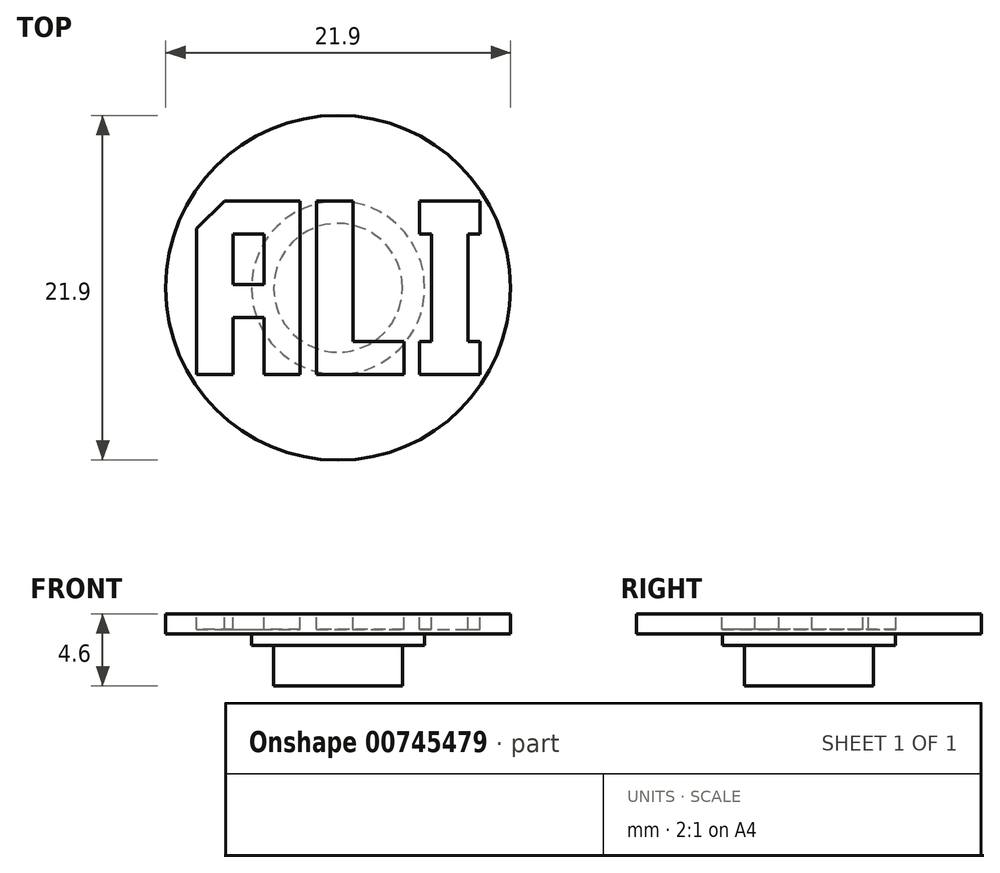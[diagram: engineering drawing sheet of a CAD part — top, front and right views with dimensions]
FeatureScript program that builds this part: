
annotation { "Feature Type Name" : "Feature", "Feature Type Description" : "" }
export const myFeature = defineFeature(function(context is Context, id is Id, definition is map)
    precondition{}
    {
        {
            var Q0;
            Q0=qCreatedBy(makeId("Top.planeOp"),FACE);
            var sketch = newSketch(context, id + "F0", { "sketchPlane" : qUnion([Q0])});
            skCircle(sketch, "E0", {"center": v(0, 0) * mm, "radius": 4.1 * mm});
            skSolve(sketch);
        }
        {
            var Q0;
            Q0 = qSketchRegion(id + "F0", true);
            extrude(context, id + "F1", {"entities" : qUnion([Q0]), "depth" : 2.6 * mm, "offsetDistance" : 25.4 * mm});
        }
        {
            var Q0;
            Q0=makeQuery(id+"F1.opExtrude","CAP_FACE",FACE,{"disambiguationData":[OSD([sQuery(id+"F0.wireOp",EDGE,"E0")])],"isStart":false});
            var sketch = newSketch(context, id + "F2", { "sketchPlane" : qUnion([Q0])});
            skCircle(sketch, "E1", {"center": v(0, 0) * mm, "radius": 5.5 * mm});
            skSolve(sketch);
        }
        {
            var Q0;
            Q0 = qSketchRegion(id + "F2", true);
            extrude(context, id + "F3", {"entities" : qUnion([Q0]), "operationType" : NewBodyOperationType.ADD, "depth" : 0.7 * mm, "offsetDistance" : 25.4 * mm});
        }
        {
            var Q0;
            Q0=makeQuery(id+"F3.opExtrude","CAP_FACE",FACE,{"disambiguationData":[OSD([sQuery(id+"F2.wireOp",EDGE,"E1")])],"isStart":false});
            var sketch = newSketch(context, id + "F4", { "sketchPlane" : qUnion([Q0])});
            skCircle(sketch, "E2", {"center": v(0, 0) * mm, "radius": 10.95 * mm});
            skSolve(sketch);
        }
        {
            var Q0;
            Q0 = qSketchRegion(id + "F4", true);
            extrude(context, id + "F5", {"entities" : qUnion([Q0]), "operationType" : NewBodyOperationType.ADD, "depth" : 1.3 * mm, "offsetDistance" : 25.4 * mm});
        }
        {
            var Q0;
            Q0=makeQuery(id+"F5.opExtrude","CAP_FACE",FACE,{"disambiguationData":[OSD([sQuery(id+"F4.wireOp",EDGE,"E2")])],"isStart":false});
            var sketch = newSketch(context, id + "F6", { "sketchPlane" : qUnion([Q0])});
            skLineSegment(sketch, "E3", {"start": v(-6.68, -5.51) * mm, "end": v(-9, -5.51) * mm});
            skLineSegment(sketch, "E4", {"start": v(-9, -5.51) * mm, "end": v(-9, 3.77) * mm});
            skLineSegment(sketch, "E5", {"start": v(-9, 3.77) * mm, "end": v(-7.22, 5.51) * mm});
            skLineSegment(sketch, "E6", {"start": v(-7.22, 5.51) * mm, "end": v(-2.4, 5.51) * mm});
            skLineSegment(sketch, "E7", {"start": v(-2.4, 5.51) * mm, "end": v(-2.4, -5.51) * mm});
            skLineSegment(sketch, "E8", {"start": v(-2.4, -5.51) * mm, "end": v(-4.71, -5.51) * mm});
            skLineSegment(sketch, "E9", {"start": v(-4.71, -5.51) * mm, "end": v(-4.71, -1.9) * mm});
            skLineSegment(sketch, "E10", {"start": v(-4.71, -1.9) * mm, "end": v(-6.68, -1.9) * mm});
            skLineSegment(sketch, "E11", {"start": v(-6.68, -1.9) * mm, "end": v(-6.68, -5.51) * mm});
            skLineSegment(sketch, "E12", {"start": v(-4.71, 0.2) * mm, "end": v(-4.71, 3.42) * mm});
            skLineSegment(sketch, "E13", {"start": v(-4.71, 3.42) * mm, "end": v(-6.68, 3.42) * mm});
            skLineSegment(sketch, "E14", {"start": v(-6.68, 3.42) * mm, "end": v(-6.68, 0.2) * mm});
            skLineSegment(sketch, "E15", {"start": v(-6.68, 0.2) * mm, "end": v(-4.71, 0.2) * mm});
            skLineSegment(sketch, "E16", {"start": v(-1.37, -5.51) * mm, "end": v(-1.37, 5.51) * mm});
            skLineSegment(sketch, "E17", {"start": v(-1.37, 5.51) * mm, "end": v(0.94, 5.51) * mm});
            skLineSegment(sketch, "E18", {"start": v(0.94, 5.51) * mm, "end": v(0.94, -3.42) * mm});
            skLineSegment(sketch, "E19", {"start": v(0.94, -3.42) * mm, "end": v(4.17, -3.42) * mm});
            skLineSegment(sketch, "E20", {"start": v(4.17, -3.42) * mm, "end": v(4.17, -5.51) * mm});
            skLineSegment(sketch, "E21", {"start": v(4.17, -5.51) * mm, "end": v(-1.37, -5.51) * mm});
            skLineSegment(sketch, "E22", {"start": v(9, -3.42) * mm, "end": v(9, -5.51) * mm});
            skLineSegment(sketch, "E23", {"start": v(9, -5.51) * mm, "end": v(5.16, -5.51) * mm});
            skLineSegment(sketch, "E24", {"start": v(5.16, -5.51) * mm, "end": v(5.16, -3.42) * mm});
            skLineSegment(sketch, "E25", {"start": v(5.16, -3.42) * mm, "end": v(5.93, -3.42) * mm});
            skLineSegment(sketch, "E26", {"start": v(5.93, -3.42) * mm, "end": v(5.93, 3.42) * mm});
            skLineSegment(sketch, "E27", {"start": v(5.93, 3.42) * mm, "end": v(5.16, 3.42) * mm});
            skLineSegment(sketch, "E28", {"start": v(5.16, 3.42) * mm, "end": v(5.16, 5.51) * mm});
            skLineSegment(sketch, "E29", {"start": v(5.16, 5.51) * mm, "end": v(9, 5.51) * mm});
            skLineSegment(sketch, "E30", {"start": v(9, 5.51) * mm, "end": v(9, 3.42) * mm});
            skLineSegment(sketch, "E31", {"start": v(9, 3.42) * mm, "end": v(8.24, 3.42) * mm});
            skLineSegment(sketch, "E32", {"start": v(8.24, 3.42) * mm, "end": v(8.24, -3.42) * mm});
            skLineSegment(sketch, "E33", {"start": v(8.24, -3.42) * mm, "end": v(9, -3.42) * mm});
            skSolve(sketch);
        }
        {
            var Q0;
            Q0 = qSketchRegion(id + "F6", true);
            extrude(context, id + "F7", {"entities" : qUnion([Q0]), "operationType" : NewBodyOperationType.REMOVE, "oppositeDirection" : true, "depth" : 1 * mm, "offsetDistance" : 25.4 * mm});
        }
    });
